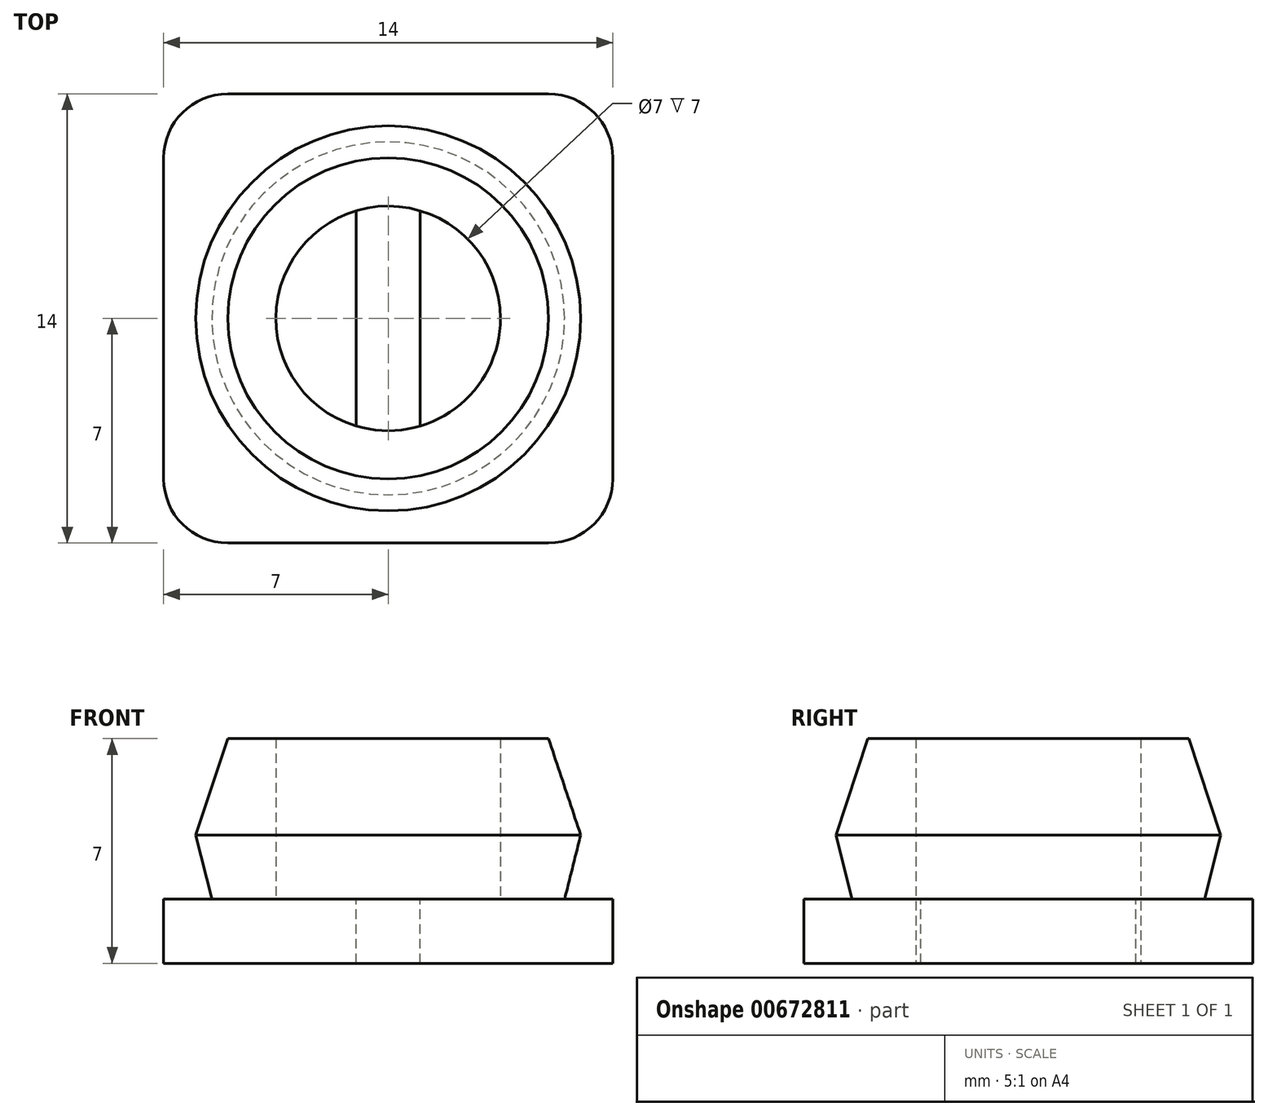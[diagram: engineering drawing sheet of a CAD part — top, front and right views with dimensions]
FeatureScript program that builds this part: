
annotation { "Feature Type Name" : "Feature", "Feature Type Description" : "" }
export const myFeature = defineFeature(function(context is Context, id is Id, definition is map)
    precondition{}
    {
        {
            var Q0;
            Q0=qCreatedBy(makeId("Top.planeOp"),FACE);
            var sketch = newSketch(context, id + "F0", { "sketchPlane" : qUnion([Q0])});
            skLineSegment(sketch, "E0.bottom", {"start": v(-14, 14) * mm, "end": v(0, 14) * mm});
            skLineSegment(sketch, "E0.top", {"start": v(-14, 0) * mm, "end": v(0, 0) * mm});
            skLineSegment(sketch, "E0.left", {"start": v(-14, 14) * mm, "end": v(-14, 0) * mm});
            skLineSegment(sketch, "E0.right", {"start": v(0, 14) * mm, "end": v(0, 0) * mm});
            skSolve(sketch);
        }
        {
            var Q0;
            Q0 = qSketchRegion(id + "F0", true);
            extrude(context, id + "F1", {"entities" : qUnion([Q0]), "depth" : 2 * mm, "offsetDistance" : 25 * mm});
        }
        {
            var Q0;
            Q0=makeQuery(id+"F1.opExtrude","CAP_FACE",FACE,{"disambiguationData":[OSD([sQuery(id+"F0.wireOp",EDGE,"E0.bottom"),sQuery(id+"F0.wireOp",EDGE,"E0.top"),sQuery(id+"F0.wireOp",EDGE,"E0.left"),sQuery(id+"F0.wireOp",EDGE,"E0.right")])],"isStart":false});
            var sketch = newSketch(context, id + "F2", { "sketchPlane" : qUnion([Q0])});
            skLineSegment(sketch, "E1.0", {"start": v(-14, 14) * mm, "end": v(0, 14) * mm});
            skLineSegment(sketch, "E2.0", {"start": v(0, 14) * mm, "end": v(0, 0) * mm});
            skLineSegment(sketch, "E3.0", {"start": v(-14, 0) * mm, "end": v(0, 0) * mm});
            skLineSegment(sketch, "E4.0", {"start": v(-14, 14) * mm, "end": v(-14, 0) * mm});
            skPoint(sketch, "E5.start.orphan", {"position": v(-14, 7) * mm});
            skPoint(sketch, "E6.start.orphan", {"position": v(0, 7) * mm});
            skLineSegment(sketch, "E7", {"start": v(-7, 14) * mm, "end": v(-7, 0) * mm, "construction": true});
            skPoint(sketch, "E8", {"position": v(16.56, -25.22) * mm});
            skPoint(sketch, "E9", {"position": v(-7, 7) * mm});
            skPoint(sketch, "E10", {"position": v(-11.31, 3) * mm});
            skPoint(sketch, "E11", {"position": v(-7.06, 6.23) * mm});
            skPoint(sketch, "E12", {"position": v(-8.84, 7) * mm});
            skCircle(sketch, "E13", {"center": v(-7, 7) * mm, "radius": 6 * mm});
            skCircle(sketch, "E14", {"center": v(-7, 7) * mm, "radius": 3.5 * mm});
            skSolve(sketch);
        }
        {
            var Q0;
            Q0=makeQuery(id+"F2.imprint","IMPRINT",FACE,{"disambiguationData":[TD([[makeQuery(id+"F2.imprint","IMPRINT",EDGE,{"derivedFrom":sQuery(id+"F2.wireOp",EDGE,"E13")}),1.0]])]});
            extrude(context, id + "F3", {"entities" : qUnion([Q0]), "operationType" : NewBodyOperationType.ADD, "depth" : 5 * mm, "offsetDistance" : 25 * mm});
        }
        {
            var Q0;
            Q0=makeQuery(id+"F3.opExtrude","CAP_EDGE",EDGE,{"disambiguationData":[OSD([sQuery(id+"F2.wireOp",EDGE,"E13")])],"isStart":false});
            chamfer(context, id + "F4", {"entities" : qUnion([Q0]), "chamferType" : ChamferType.TWO_OFFSETS, "width1" : 1 * mm, "oppositeDirection" : false, "width2" : 3 * mm, "tangentPropagation" : true});
        }
        {
            var Q0;
            Q0=makeQuery(id+"F1.opExtrude","SWEPT_BODY",BODY,{"disambiguationData":[OSD([sQuery(id+"F0.wireOp",EDGE,"E0.bottom"),sQuery(id+"F0.wireOp",EDGE,"E0.top"),sQuery(id+"F0.wireOp",EDGE,"E0.left"),sQuery(id+"F0.wireOp",EDGE,"E0.right")])]});
            var Q1;
            Q1=sQuery(id+"F2.wireOp",VERTEX,"E6.start.orphan");
            var Q2;
            Q2=sQuery(id+"F2.wireOp",EDGE,"E3.0");
            transform(context, id + "F5", {"entities" : qUnion([Q0]), "transformType" : TransformType.TRANSLATION_3D, "dx" : 7 * mm, "dy" : 0 * mm, "dz" : 0 * mm, "makeCopy" : false});
        }
        {
            var Q0;
            Q0=qCreatedBy(makeId("Right.planeOp"),FACE);
            var sketch = newSketch(context, id + "F6", { "sketchPlane" : qUnion([Q0])});
            skLineSegment(sketch, "E15", {"start": v(0, -3.47) * mm, "end": v(0, 24.03) * mm});
            skLineSegment(sketch, "E16", {"start": v(13, 4) * mm, "end": v(12, 7) * mm});
            skLineSegment(sketch, "E17", {"start": v(2, 7) * mm, "end": v(1, 4) * mm});
            skLineSegment(sketch, "E18", {"start": v(13, 4) * mm, "end": v(13, 2) * mm});
            skLineSegment(sketch, "E19", {"start": v(1, 2) * mm, "end": v(1, 4) * mm});
            skLineSegment(sketch, "E20", {"start": v(3.5, 7) * mm, "end": v(2, 7) * mm});
            skLineSegment(sketch, "E21", {"start": v(12, 7) * mm, "end": v(10.5, 7) * mm});
            skLineSegment(sketch, "E22", {"start": v(10.5, 7) * mm, "end": v(10.5, 2) * mm});
            skLineSegment(sketch, "E23", {"start": v(3.5, 2) * mm, "end": v(3.5, 7) * mm});
            skLineSegment(sketch, "E24", {"start": v(1, 2) * mm, "end": v(0, 2) * mm});
            skLineSegment(sketch, "E25", {"start": v(14, 2) * mm, "end": v(13, 2) * mm});
            skLineSegment(sketch, "E26", {"start": v(10.5, 2) * mm, "end": v(3.5, 2) * mm});
            skLineSegment(sketch, "E27", {"start": v(14, 0) * mm, "end": v(14, 2) * mm});
            skLineSegment(sketch, "E28", {"start": v(13, 4) * mm, "end": v(12.5, 2) * mm});
            skLineSegment(sketch, "E29", {"start": v(13, 2) * mm, "end": v(12.5, 2) * mm});
            skLineSegment(sketch, "E30", {"start": v(12.75, 2) * mm, "end": v(12.75, 2) * mm});
            skPoint(sketch, "E31.end.orphan", {"position": v(12.75, 2.4) * mm});
            skPoint(sketch, "E32.0", {"position": v(7, 2) * mm});
            skLineSegment(sketch, "E33", {"start": v(7, 2) * mm, "end": v(7, 43.83) * mm});
            skSolve(sketch);
        }
        {
            var Q0;
            Q0=makeQuery(id+"F6.imprint","IMPRINT",FACE,{"disambiguationData":[TD([[makeQuery(id+"F6.imprint","IMPRINT",EDGE,{"derivedFrom":sQuery(id+"F6.wireOp",EDGE,"E18")}),-1.0]])]});
            var Q1;
            Q1=sQuery(id+"F6.wireOp",EDGE,"E33");
            revolve(context, id + "F7", {"operationType" : NewBodyOperationType.REMOVE, "entities" : qUnion([Q0]), "axis" : qUnion([Q1]), "revolveType" : RevolveType.FULL, "oppositeDirection" : true});
        }
        {
            var Q0;
            Q0=makeQuery(id+"F3.boolean.opBoolean","SPLIT",FACE,{"disambiguationData":[TD([makeQuery(id+"F3.opExtrude","SWEPT_FACE",FACE,{"disambiguationData":[OSD([sQuery(id+"F2.wireOp",EDGE,"E14")])]})])],"derivedFrom":makeQuery(id+"F1.opExtrude","CAP_FACE",FACE,{"disambiguationData":[OSD([sQuery(id+"F0.wireOp",EDGE,"E0.bottom"),sQuery(id+"F0.wireOp",EDGE,"E0.top"),sQuery(id+"F0.wireOp",EDGE,"E0.left"),sQuery(id+"F0.wireOp",EDGE,"E0.right")])],"isStart":false})});
            var sketch = newSketch(context, id + "F8", { "sketchPlane" : qUnion([Q0])});
            skCircle(sketch, "E34.0", {"center": v(0, 7) * mm, "radius": 3.5 * mm});
            skLineSegment(sketch, "E35", {"start": v(1, 10.35) * mm, "end": v(1, 3.65) * mm});
            skLineSegment(sketch, "E36", {"start": v(-1, 10.35) * mm, "end": v(-1, 3.65) * mm});
            skSolve(sketch);
        }
        {
            var Q0;
            {var subQ0=sQuery(id+"F8.wireOp",EDGE,"E35");Q0=makeQuery(id+"F8.imprint","IMPRINT",FACE,{"disambiguationData":[TD([[makeQuery(id+"F8.imprint","IMPRINT",EDGE,{"derivedFrom":subQ0}),-1.0]])]});}
            extrude(context, id + "F9", {"entities" : qUnion([Q0]), "operationType" : NewBodyOperationType.REMOVE, "endBound" : BoundingType.UP_TO_NEXT, "oppositeDirection" : true, "depth" : 25 * mm, "offsetDistance" : 25 * mm});
        }
        {
            var Q0;
            Q0=makeQuery(id+"F1.opExtrude","SWEPT_EDGE",EDGE,{"disambiguationData":[OSD([sQuery(id+"F0.wireOp",EDGE,"E0.top"),sQuery(id+"F0.wireOp",EDGE,"E0.right")])]});
            var Q1;
            Q1=makeQuery(id+"F1.opExtrude","SWEPT_EDGE",EDGE,{"disambiguationData":[OSD([sQuery(id+"F0.wireOp",EDGE,"E0.bottom"),sQuery(id+"F0.wireOp",EDGE,"E0.right")])]});
            var Q2;
            Q2=makeQuery(id+"F1.opExtrude","SWEPT_EDGE",EDGE,{"disambiguationData":[OSD([sQuery(id+"F0.wireOp",EDGE,"E0.bottom"),sQuery(id+"F0.wireOp",EDGE,"E0.left")])]});
            var Q3;
            Q3=makeQuery(id+"F1.opExtrude","SWEPT_EDGE",EDGE,{"disambiguationData":[OSD([sQuery(id+"F0.wireOp",EDGE,"E0.top"),sQuery(id+"F0.wireOp",EDGE,"E0.left")])]});
            fillet(context, id + "F10", {"entities" : qUnion([Q0, Q1, Q2, Q3]), "radius" : 2 * mm, "tangentPropagation" : true, "allowEdgeOverflow" : false});
        }
    });
